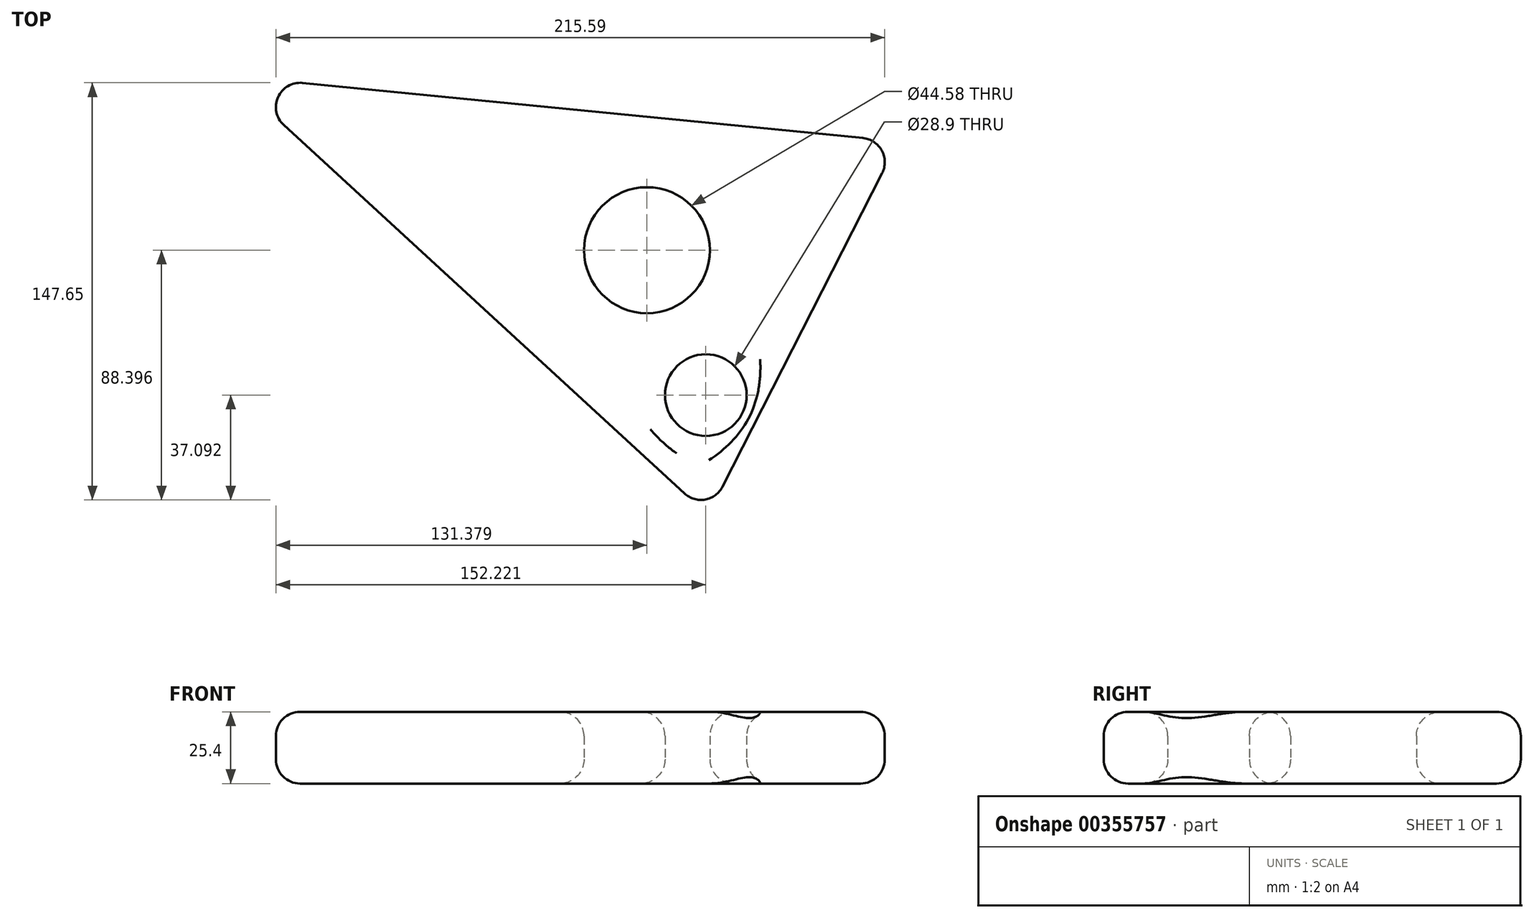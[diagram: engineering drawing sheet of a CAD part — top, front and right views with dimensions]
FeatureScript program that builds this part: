
annotation { "Feature Type Name" : "Feature", "Feature Type Description" : "" }
export const myFeature = defineFeature(function(context is Context, id is Id, definition is map)
    precondition{}
    {
        {
            var Q0;
            Q0=qCreatedBy(makeId("Top.planeOp"),FACE);
            var sketch = newSketch(context, id + "F0", { "sketchPlane" : qUnion([Q0])});
            skLineSegment(sketch, "E0", {"start": v(55.31, -85.78) * mm, "end": v(122.65, 46.5) * mm});
            skLineSegment(sketch, "E1", {"start": v(122.65, 46.5) * mm, "end": v(-113.83, 69.74) * mm});
            skLineSegment(sketch, "E2", {"start": v(-113.83, 69.74) * mm, "end": v(55.31, -85.78) * mm});
            skCircle(sketch, "E3", {"center": v(54.51, -43.29) * mm, "radius": 14.45 * mm});
            skCircle(sketch, "E4", {"center": v(33.67, 8.02) * mm, "radius": 22.29 * mm});
            skArc(sketch, "E5", {"start": v(-25.64, 61.07) * mm, "mid": v(-12, 45.43) * mm, "end": v(4.4, 58.12) * mm});
            skArc(sketch, "E6", {"start": v(-95.42, 67.93) * mm, "mid": v(-87.5, 58.35) * mm, "end": v(-77.87, 66.2) * mm});
            skArc(sketch, "E7", {"start": v(112.4, 26.35) * mm, "mid": v(88.9, 21.72) * mm, "end": v(98.98, 0) * mm});
            skSolve(sketch);
        }
        {
            var Q0;
            Q0 = qSketchRegion(id + "F0", true);
            extrude(context, id + "F1", {"entities" : qUnion([Q0]), "depth" : 25.4 * mm});
        }
        {
            var Q0;
            Q0=makeQuery(id+"F1.opExtrude","CAP_EDGE",EDGE,{"disambiguationData":[OSD([sQuery(id+"F0.wireOp",EDGE,"E1")])],"isStart":false});
            var Q1;
            Q1=makeQuery(id+"F1.opExtrude","CAP_EDGE",EDGE,{"disambiguationData":[OSD([sQuery(id+"F0.wireOp",EDGE,"E2")])],"isStart":false});
            var Q2;
            Q2=makeQuery(id+"F1.opExtrude","SWEPT_FACE",FACE,{"disambiguationData":[OSD([sQuery(id+"F0.wireOp",EDGE,"E2")])]});
            var Q3;
            Q3=makeQuery(id+"F1.opExtrude","CAP_FACE",FACE,{"disambiguationData":[OSD([sQuery(id+"F0.wireOp",EDGE,"E0"),sQuery(id+"F0.wireOp",EDGE,"E1"),sQuery(id+"F0.wireOp",EDGE,"E2"),sQuery(id+"F0.wireOp",EDGE,"E3"),sQuery(id+"F0.wireOp",EDGE,"E4")])],"isStart":true});
            var Q4;
            Q4=makeQuery(id+"F1.opExtrude","CAP_EDGE",EDGE,{"disambiguationData":[OSD([sQuery(id+"F0.wireOp",EDGE,"E3")])],"isStart":false});
            var Q5;
            Q5=makeQuery(id+"F1.opExtrude","CAP_EDGE",EDGE,{"disambiguationData":[OSD([sQuery(id+"F0.wireOp",EDGE,"E3")])],"isStart":true});
            var Q6;
            Q6=makeQuery(id+"F1.opExtrude","SWEPT_FACE",FACE,{"disambiguationData":[OSD([sQuery(id+"F0.wireOp",EDGE,"E4")])]});
            var Q7;
            Q7=makeQuery(id+"F1.opExtrude","CAP_EDGE",EDGE,{"disambiguationData":[OSD([sQuery(id+"F0.wireOp",EDGE,"E0")])],"isStart":false});
            var Q8;
            Q8=makeQuery(id+"F1.opExtrude","SWEPT_FACE",FACE,{"disambiguationData":[OSD([sQuery(id+"F0.wireOp",EDGE,"E0")])]});
            var Q9;
            Q9=makeQuery(id+"F1.opExtrude","CAP_FACE",FACE,{"disambiguationData":[OSD([sQuery(id+"F0.wireOp",EDGE,"E0"),sQuery(id+"F0.wireOp",EDGE,"E1"),sQuery(id+"F0.wireOp",EDGE,"E2"),sQuery(id+"F0.wireOp",EDGE,"E3"),sQuery(id+"F0.wireOp",EDGE,"E4")])],"isStart":false});
            var Q10;
            Q10=makeQuery(id+"F1.opExtrude","CAP_EDGE",EDGE,{"disambiguationData":[OSD([sQuery(id+"F0.wireOp",EDGE,"E1")])],"isStart":true});
            var Q11;
            Q11=makeQuery(id+"F1.opExtrude","SWEPT_FACE",FACE,{"disambiguationData":[OSD([sQuery(id+"F0.wireOp",EDGE,"E3")])]});
            var Q12;
            Q12=makeQuery(id+"F1.opExtrude","SWEPT_FACE",FACE,{"disambiguationData":[OSD([sQuery(id+"F0.wireOp",EDGE,"E1")])]});
            var Q13;
            Q13=makeQuery(id+"F1.opExtrude","CAP_EDGE",EDGE,{"disambiguationData":[OSD([sQuery(id+"F0.wireOp",EDGE,"E4")])],"isStart":false});
            var Q14;
            Q14=makeQuery(id+"F1.opExtrude","CAP_EDGE",EDGE,{"disambiguationData":[OSD([sQuery(id+"F0.wireOp",EDGE,"E4")])],"isStart":true});
            var Q15;
            Q15=makeQuery(id+"F1.opExtrude","SWEPT_EDGE",EDGE,{"disambiguationData":[OSD([sQuery(id+"F0.wireOp",EDGE,"E1"),sQuery(id+"F0.wireOp",EDGE,"E2")])]});
            var Q16;
            Q16=makeQuery(id+"F1.opExtrude","SWEPT_EDGE",EDGE,{"disambiguationData":[OSD([sQuery(id+"F0.wireOp",EDGE,"E0"),sQuery(id+"F0.wireOp",EDGE,"E1")])]});
            var Q17;
            Q17=makeQuery(id+"F1.opExtrude","SWEPT_EDGE",EDGE,{"disambiguationData":[OSD([sQuery(id+"F0.wireOp",EDGE,"E0"),sQuery(id+"F0.wireOp",EDGE,"E2")])]});
            var Q18;
            Q18=makeQuery(id+"F1.opExtrude","CAP_EDGE",EDGE,{"disambiguationData":[OSD([sQuery(id+"F0.wireOp",EDGE,"E2")])],"isStart":true});
            var Q19;
            Q19=makeQuery(id+"F1.opExtrude","CAP_EDGE",EDGE,{"disambiguationData":[OSD([sQuery(id+"F0.wireOp",EDGE,"E0")])],"isStart":true});
            fillet(context, id + "F2", {"entities" : qUnion([Q0, Q1, Q2, Q3, Q4, Q5, Q6, Q7, Q8, Q9, Q10, Q11, Q12, Q13, Q14, Q15, Q16, Q17, Q18, Q19]), "radius" : 8.58 * mm, "tangentPropagation" : true, "allowEdgeOverflow" : false});
        }
    });
